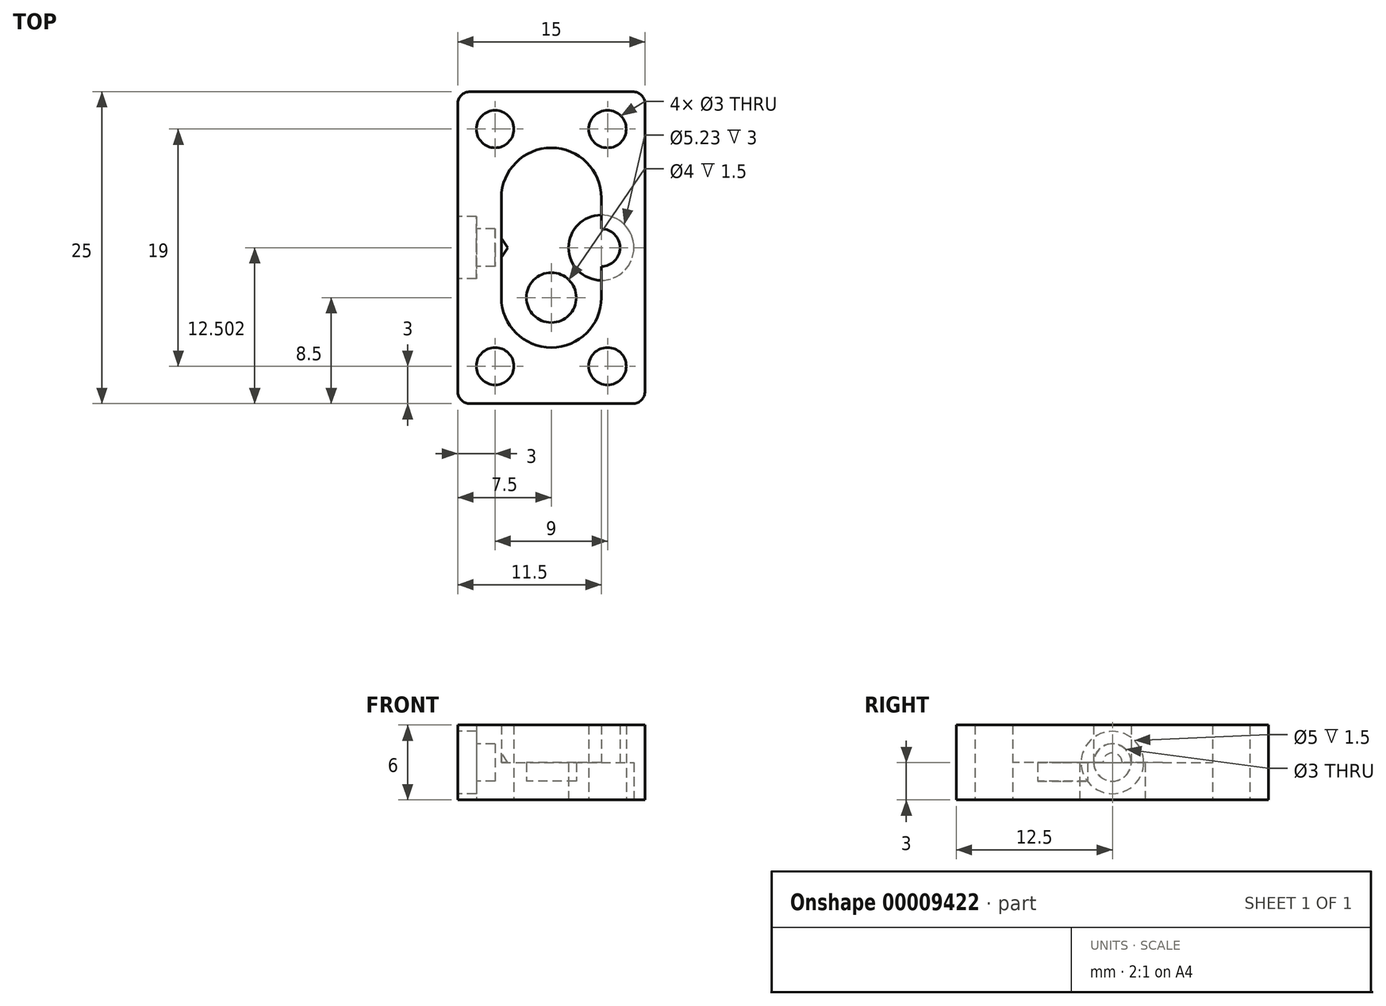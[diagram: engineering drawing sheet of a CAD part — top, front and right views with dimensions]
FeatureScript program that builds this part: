
annotation { "Feature Type Name" : "Feature", "Feature Type Description" : "" }
export const myFeature = defineFeature(function(context is Context, id is Id, definition is map)
    precondition{}
    {
        {
            var Q0;
            Q0=qCreatedBy(makeId("Top.planeOp"),FACE);
            var sketch = newSketch(context, id + "F0", { "sketchPlane" : qUnion([Q0])});
            skLineSegment(sketch, "E0.rect.bottom", {"start": v(-6.5, 12.5) * mm, "end": v(6.5, 12.5) * mm});
            skLineSegment(sketch, "E0.rect.top", {"start": v(-6.5, -12.5) * mm, "end": v(6.5, -12.5) * mm});
            skLineSegment(sketch, "E0.rect.left", {"start": v(-7.5, 11.5) * mm, "end": v(-7.5, -11.5) * mm});
            skLineSegment(sketch, "E0.rect.right", {"start": v(7.5, 11.5) * mm, "end": v(7.5, -11.5) * mm});
            skPoint(sketch, "E0.rect.middle", {"position": v(0, 0) * mm});
            skCircle(sketch, "E1", {"center": v(-4.5, 9.5) * mm, "radius": 1.5 * mm});
            skCircle(sketch, "E2.0.1.0", {"center": v(-4.5, -9.5) * mm, "radius": 1.5 * mm});
            skCircle(sketch, "E2.1.0.0", {"center": v(4.5, 9.5) * mm, "radius": 1.5 * mm});
            skCircle(sketch, "E2.1.1.0", {"center": v(4.5, -9.5) * mm, "radius": 1.5 * mm});
            skLineSegment(sketch, "E2.direction1", {"start": v(-4.5, 9.5) * mm, "end": v(4.5, 9.5) * mm, "construction": true});
            skLineSegment(sketch, "E2.direction2", {"start": v(-4.5, 9.5) * mm, "end": v(-4.5, -9.5) * mm, "construction": true});
            skPoint(sketch, "E3.visualSharp", {"position": v(-7.5, 12.5) * mm});
            skArc(sketch, "E3.filletArc", {"start": v(-6.5, 12.5) * mm, "mid": v(-7.2, 12.2) * mm, "end": v(-7.5, 11.5) * mm});
            skPoint(sketch, "E4.visualSharp", {"position": v(7.5, 12.5) * mm});
            skArc(sketch, "E4.filletArc", {"start": v(7.5, 11.5) * mm, "mid": v(7.2, 12.2) * mm, "end": v(6.5, 12.5) * mm});
            skPoint(sketch, "E5.visualSharp", {"position": v(7.5, -12.5) * mm});
            skArc(sketch, "E5.filletArc", {"start": v(6.5, -12.5) * mm, "mid": v(7.2, -12.2) * mm, "end": v(7.5, -11.5) * mm});
            skPoint(sketch, "E6.visualSharp", {"position": v(-7.5, -12.5) * mm});
            skArc(sketch, "E6.filletArc", {"start": v(-7.5, -11.5) * mm, "mid": v(-7.2, -12.2) * mm, "end": v(-6.5, -12.5) * mm});
            skLineSegment(sketch, "E7", {"start": v(0, 19.5) * mm, "end": v(0, -16.06) * mm, "construction": true});
            skArc(sketch, "E8", {"start": v(4, 4) * mm, "mid": v(0, 8) * mm, "end": v(-4, 4) * mm});
            skArc(sketch, "E9", {"start": v(-4, -4) * mm, "mid": v(0, -8) * mm, "end": v(4, -4) * mm});
            skLineSegment(sketch, "E10", {"start": v(-4, 4) * mm, "end": v(-4, -4) * mm});
            skLineSegment(sketch, "E11", {"start": v(4, 4) * mm, "end": v(4, 1.5) * mm});
            skArc(sketch, "E12", {"start": v(4, -1.5) * mm, "mid": v(5.5, 0) * mm, "end": v(4, 1.5) * mm});
            skCircle(sketch, "E13", {"center": v(0, -4) * mm, "radius": 2 * mm});
            skLineSegment(sketch, "E14.trimOffspring", {"start": v(4, -1.5) * mm, "end": v(4, -4) * mm});
            skCircle(sketch, "E15", {"center": v(4, 0) * mm, "radius": 2.61 * mm});
            skSolve(sketch);
        }
        {
            var Q0;
            Q0=makeQuery(id+"F0.imprint","IMPRINT",FACE,{"disambiguationData":[TD([[makeQuery(id+"F0.imprint","IMPRINT",EDGE,{"derivedFrom":sQuery(id+"F0.wireOp",EDGE,"E0.rect.bottom")}),-1.0]])]});
            var Q1;
            {var subQ5=sQuery(id+"F0.wireOp",EDGE,"E12");Q1=makeQuery(id+"F0.imprint","IMPRINT",FACE,{"disambiguationData":[TD([[makeQuery(id+"F0.imprint","IMPRINT",EDGE,{"derivedFrom":subQ5}),-1.0]])]});}
            extrude(context, id + "F1", {"entities" : qUnion([Q0, Q1]), "depth" : 6 * mm});
        }
        {
            var Q0;
            Q0 = qSketchRegion(id + "F0", true);
            var Q1;
            {var subQ2=sQuery(id+"F0.wireOp",EDGE,"E8");Q1=makeQuery(id+"F0.imprint","IMPRINT",FACE,{"disambiguationData":[TD([[makeQuery(id+"F0.imprint","IMPRINT",EDGE,{"derivedFrom":subQ2}),1.0]])]});}
            extrude(context, id + "F2", {"entities" : qUnion([Q0, Q1]), "operationType" : NewBodyOperationType.ADD, "depth" : 3 * mm});
        }
        {
            var Q0;
            Q0=makeQuery(id+"F0.imprint","IMPRINT",FACE,{"disambiguationData":[TD([[makeQuery(id+"F0.imprint","IMPRINT",EDGE,{"derivedFrom":sQuery(id+"F0.wireOp",EDGE,"E13")}),1.0]])]});
            extrude(context, id + "F3", {"entities" : qUnion([Q0]), "operationType" : NewBodyOperationType.ADD, "depth" : 1.5 * mm});
        }
        {
            var Q0;
            {var subQ5=sQuery(id+"F0.wireOp",EDGE,"E12");Q0=makeQuery(id+"F0.imprint","IMPRINT",FACE,{"disambiguationData":[TD([[makeQuery(id+"F0.imprint","IMPRINT",EDGE,{"derivedFrom":subQ5}),-1.0]])]});}
            extrude(context, id + "F4", {"entities" : qUnion([Q0]), "operationType" : NewBodyOperationType.REMOVE, "depth" : 3 * mm});
        }
        {
            var Q0;
            Q0=makeQuery(id+"F1.opExtrude","SWEPT_FACE",FACE,{"disambiguationData":[OSD([sQuery(id+"F0.wireOp",EDGE,"E0.rect.left")])]});
            var sketch = newSketch(context, id + "F5", { "sketchPlane" : qUnion([Q0])});
            skCircle(sketch, "E16", {"center": v(0, 3) * mm, "radius": 2.5 * mm});
            skCircle(sketch, "E17", {"center": v(0, 3) * mm, "radius": 1.5 * mm});
            skSolve(sketch);
        }
        {
            var Q0;
            Q0=makeQuery(id+"F5.imprint","IMPRINT",FACE,{"disambiguationData":[TD([[makeQuery(id+"F5.imprint","IMPRINT",EDGE,{"derivedFrom":sQuery(id+"F5.wireOp",EDGE,"E17")}),1.0]])]});
            extrude(context, id + "F6", {"entities" : qUnion([Q0]), "operationType" : NewBodyOperationType.REMOVE, "oppositeDirection" : true, "depth" : 3 * mm});
        }
        {
            var Q0;
            Q0=makeQuery(id+"F5.imprint","IMPRINT",FACE,{"disambiguationData":[TD([[makeQuery(id+"F5.imprint","IMPRINT",EDGE,{"derivedFrom":sQuery(id+"F5.wireOp",EDGE,"E16")}),1.0]])]});
            extrude(context, id + "F7", {"entities" : qUnion([Q0]), "operationType" : NewBodyOperationType.REMOVE, "oppositeDirection" : true, "depth" : 1.5 * mm});
        }
        {
            var Q0;
            Q0=makeQuery(id+"F2.opExtrude","CAP_FACE",FACE,{"disambiguationData":[OSD([sQuery(id+"F0.wireOp",EDGE,"E0.rect.bottom"),sQuery(id+"F0.wireOp",EDGE,"E0.rect.top"),sQuery(id+"F0.wireOp",EDGE,"E0.rect.left"),sQuery(id+"F0.wireOp",EDGE,"E0.rect.right"),sQuery(id+"F0.wireOp",EDGE,"E1"),sQuery(id+"F0.wireOp",EDGE,"E2.0.1.0"),sQuery(id+"F0.wireOp",EDGE,"E2.1.0.0"),sQuery(id+"F0.wireOp",EDGE,"E2.1.1.0"),sQuery(id+"F0.wireOp",EDGE,"E3.filletArc"),sQuery(id+"F0.wireOp",EDGE,"E4.filletArc"),sQuery(id+"F0.wireOp",EDGE,"E5.filletArc"),sQuery(id+"F0.wireOp",EDGE,"E6.filletArc"),sQuery(id+"F0.wireOp",EDGE,"E13"),sQuery(id+"F0.wireOp",EDGE,"E15")])],"isStart":false});
            var sketch = newSketch(context, id + "F8", { "sketchPlane" : qUnion([Q0])});
            skLineSegment(sketch, "E18", {"start": v(-3.48, 0) * mm, "end": v(-4.5, 0) * mm});
            skLineSegment(sketch, "E19", {"start": v(-4.5, 0) * mm, "end": v(-4.5, 1.5) * mm});
            skLineSegment(sketch, "E20", {"start": v(-4.5, 1.5) * mm, "end": v(-3.48, 0) * mm});
            skSolve(sketch);
        }
        {
            var Q0;
            {var subQ5=sQuery(id+"F8.wireOp",EDGE,"E19");Q0=makeQuery(id+"F8.imprint","IMPRINT",FACE,{"disambiguationData":[TD([[makeQuery(id+"F8.imprint","IMPRINT",EDGE,{"derivedFrom":subQ5}),-1.0]])]});}
            var Q1;
            {var subQ1=sQuery(id+"F8.wireOp",EDGE,"E20");var subQ3=sQuery(id+"F8.wireOp",EDGE,"E18");var subQ5=makeQuery(id+"F8.imprint","INTERSECT",VERTEX,{"derivedFrom":[subQ3,subQ1]});Q1=makeQuery(id+"F8.imprint","IMPRINT",FACE,{"disambiguationData":[TD([[makeQuery(id+"F8.imprint","IMPRINT",EDGE,{"disambiguationData":[TD([[subQ5,-1.0]])],"derivedFrom":subQ3}),-1.0]])]});}
            var Q2;
            Q2=sQuery(id+"F8.wireOp",EDGE,"E18");
            revolve(context, id + "F9", {"operationType" : NewBodyOperationType.REMOVE, "entities" : qUnion([Q0, Q1]), "axis" : qUnion([Q2]), "revolveType" : RevolveType.FULL, "oppositeDirection" : true});
        }
    });
